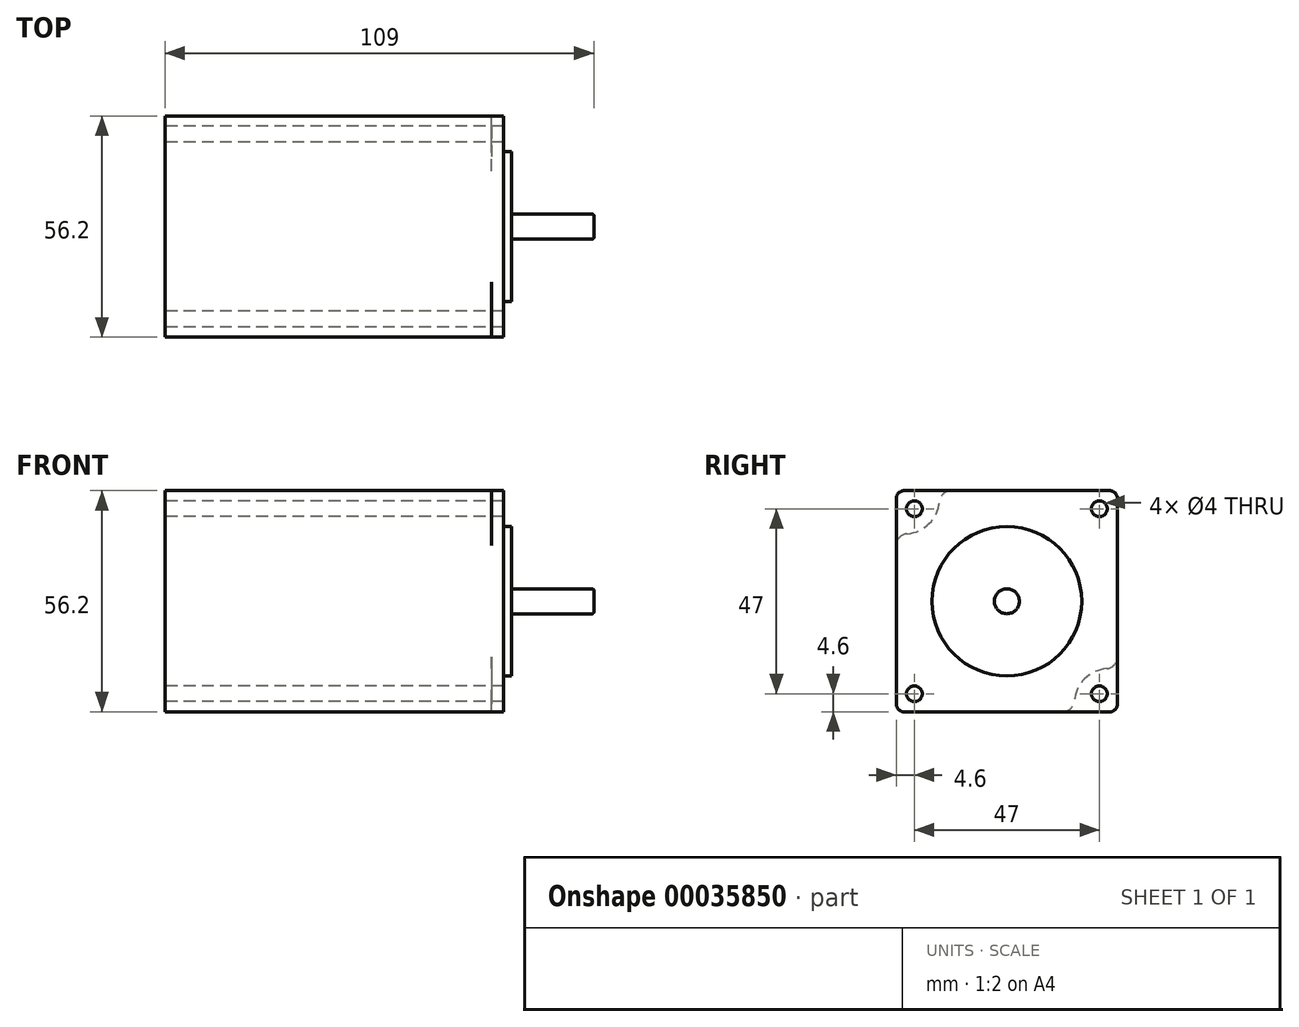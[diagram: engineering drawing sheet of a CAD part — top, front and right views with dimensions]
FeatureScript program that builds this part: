
annotation { "Feature Type Name" : "Feature", "Feature Type Description" : "" }
export const myFeature = defineFeature(function(context is Context, id is Id, definition is map)
    precondition{}
    {
        {
            var Q0;
            Q0=qCreatedBy(makeId("Right.planeOp"),FACE);
            var sketch = newSketch(context, id + "F0", { "sketchPlane" : qUnion([Q0])});
            skLineSegment(sketch, "E0.bottom", {"start": v(-26.1, 28.1) * mm, "end": v(26.1, 28.1) * mm});
            skLineSegment(sketch, "E0.top", {"start": v(-26.1, -28.1) * mm, "end": v(26.1, -28.1) * mm});
            skLineSegment(sketch, "E0.left", {"start": v(-28.1, 26.1) * mm, "end": v(-28.1, -26.1) * mm});
            skLineSegment(sketch, "E0.right", {"start": v(28.1, 26.1) * mm, "end": v(28.1, -26.1) * mm});
            skLineSegment(sketch, "E1", {"start": v(-28.1, 0) * mm, "end": v(28.1, 0) * mm, "construction": true});
            skLineSegment(sketch, "E2", {"start": v(0, 28.1) * mm, "end": v(0, -28.1) * mm, "construction": true});
            skCircle(sketch, "E3", {"center": v(-23.5, 23.5) * mm, "radius": 2 * mm});
            skCircle(sketch, "E4.0.MirrorC", {"center": v(23.5, 23.5) * mm, "radius": 2 * mm});
            skCircle(sketch, "E5.0.MirrorC", {"center": v(23.5, -23.5) * mm, "radius": 2 * mm});
            skCircle(sketch, "E6.0.MirrorC", {"center": v(-23.5, -23.5) * mm, "radius": 2 * mm});
            skPoint(sketch, "E7.visualSharp", {"position": v(-28.1, 28.1) * mm});
            skArc(sketch, "E7.filletArc", {"start": v(-26.1, 28.1) * mm, "mid": v(-27.51, 27.51) * mm, "end": v(-28.1, 26.1) * mm});
            skPoint(sketch, "E8.visualSharp", {"position": v(28.1, 28.1) * mm});
            skArc(sketch, "E8.filletArc", {"start": v(28.1, 26.1) * mm, "mid": v(27.51, 27.51) * mm, "end": v(26.1, 28.1) * mm});
            skPoint(sketch, "E9.visualSharp", {"position": v(28.1, -28.1) * mm});
            skArc(sketch, "E9.filletArc", {"start": v(26.1, -28.1) * mm, "mid": v(27.51, -27.51) * mm, "end": v(28.1, -26.1) * mm});
            skPoint(sketch, "E10.visualSharp", {"position": v(-28.1, -28.1) * mm});
            skArc(sketch, "E10.filletArc", {"start": v(-28.1, -26.1) * mm, "mid": v(-27.51, -27.51) * mm, "end": v(-26.1, -28.1) * mm});
            skLineSegment(sketch, "E11", {"start": v(23.5, 23.5) * mm, "end": v(-23.5, 23.5) * mm, "construction": true});
            skLineSegment(sketch, "E12", {"start": v(-23.5, 23.5) * mm, "end": v(-23.5, -23.5) * mm, "construction": true});
            skLineSegment(sketch, "E13", {"start": v(28.1, 28.1) * mm, "end": v(-28.1, 28.1) * mm, "construction": true});
            skLineSegment(sketch, "E14", {"start": v(-28.1, -28.1) * mm, "end": v(-28.1, 28.1) * mm, "construction": true});
            skSolve(sketch);
        }
        {
            var Q0;
            Q0=makeQuery(id+"F0.imprint","IMPRINT",FACE,{"disambiguationData":[TD([[makeQuery(id+"F0.imprint","IMPRINT",EDGE,{"derivedFrom":sQuery(id+"F0.wireOp",EDGE,"E0.bottom")}),-1.0]])]});
            extrude(context, id + "F1", {"entities" : qUnion([Q0]), "depth" : 86 * mm});
        }
        {
            var Q0;
            Q0=makeQuery(id+"F1.opExtrude","CAP_FACE",FACE,{"disambiguationData":[OSD([sQuery(id+"F0.wireOp",EDGE,"E0.bottom"),sQuery(id+"F0.wireOp",EDGE,"E0.top"),sQuery(id+"F0.wireOp",EDGE,"E0.left"),sQuery(id+"F0.wireOp",EDGE,"E0.right"),sQuery(id+"F0.wireOp",EDGE,"E3"),sQuery(id+"F0.wireOp",EDGE,"E4.0.MirrorC"),sQuery(id+"F0.wireOp",EDGE,"E5.0.MirrorC"),sQuery(id+"F0.wireOp",EDGE,"E6.0.MirrorC"),sQuery(id+"F0.wireOp",EDGE,"E7.filletArc"),sQuery(id+"F0.wireOp",EDGE,"E8.filletArc"),sQuery(id+"F0.wireOp",EDGE,"E9.filletArc"),sQuery(id+"F0.wireOp",EDGE,"E10.filletArc"),sQuery(id+"F0.wireOp",EDGE,"ba6df332-af28-43ae-9241-533709e672ff")])],"isStart":false});
            var sketch = newSketch(context, id + "F2", { "sketchPlane" : qUnion([Q0])});
            skCircle(sketch, "E15", {"center": v(0, 0) * mm, "radius": 19 * mm});
            skSolve(sketch);
        }
        {
            var Q0;
            {var subQ0=makeQuery(id+"F2.imprint","IMPRINT",EDGE,{"derivedFrom":makeQuery(id+"F1.opExtrude","CAP_EDGE",EDGE,{"disambiguationData":[OSD([sQuery(id+"F0.wireOp",EDGE,"ba6df332-af28-43ae-9241-533709e672ff")])],"isStart":false})});Q0=qUnion([makeQuery(id+"F2.imprint","IMPRINT",FACE,{"disambiguationData":[TD([[subQ0,1.0]])]}),makeQuery(id+"F2.imprint","IMPRINT",FACE,{"disambiguationData":[TD([[makeQuery(id+"F2.imprint","IMPRINT",EDGE,{"derivedFrom":sQuery(id+"F2.wireOp",EDGE,"E15")}),1.0]])]})]);}
            extrude(context, id + "F3", {"entities" : qUnion([Q0]), "operationType" : NewBodyOperationType.ADD, "depth" : 2 * mm});
        }
        {
            var Q0;
            Q0=makeQuery(id+"F3.opExtrude","CAP_FACE",FACE,{"disambiguationData":[OSD([sQuery(id+"F2.wireOp",EDGE,"E15")])],"isStart":false});
            var sketch = newSketch(context, id + "F4", { "sketchPlane" : qUnion([Q0])});
            skCircle(sketch, "E16", {"center": v(0, 0) * mm, "radius": 3.17 * mm});
            skSolve(sketch);
        }
        {
            var Q0;
            Q0=makeQuery(id+"F4.imprint","IMPRINT",FACE,{"disambiguationData":[TD([[makeQuery(id+"F4.imprint","IMPRINT",EDGE,{"derivedFrom":sQuery(id+"F4.wireOp",EDGE,"E16")}),1.0]])]});
            extrude(context, id + "F5", {"entities" : qUnion([Q0]), "operationType" : NewBodyOperationType.ADD, "depth" : 21 * mm});
        }
        {
            var Q0;
            Q0=makeQuery(id+"F5.opExtrude","CAP_EDGE",EDGE,{"disambiguationData":[OSD([sQuery(id+"F4.wireOp",EDGE,"E16")])],"isStart":false});
            fillet(context, id + "F6", {"entities" : qUnion([Q0]), "radius" : 0.5 * mm, "tangentPropagation" : true, "allowEdgeOverflow" : false});
        }
        {
            var Q0;
            Q0=makeQuery(id+"F1.opExtrude","CAP_FACE",FACE,{"disambiguationData":[OSD([sQuery(id+"F0.wireOp",EDGE,"E0.bottom"),sQuery(id+"F0.wireOp",EDGE,"E0.top"),sQuery(id+"F0.wireOp",EDGE,"E0.left"),sQuery(id+"F0.wireOp",EDGE,"E0.right"),sQuery(id+"F0.wireOp",EDGE,"E3"),sQuery(id+"F0.wireOp",EDGE,"E4.0.MirrorC"),sQuery(id+"F0.wireOp",EDGE,"E5.0.MirrorC"),sQuery(id+"F0.wireOp",EDGE,"E6.0.MirrorC"),sQuery(id+"F0.wireOp",EDGE,"E7.filletArc"),sQuery(id+"F0.wireOp",EDGE,"E8.filletArc"),sQuery(id+"F0.wireOp",EDGE,"E9.filletArc"),sQuery(id+"F0.wireOp",EDGE,"E10.filletArc"),sQuery(id+"F0.wireOp",EDGE,"ba6df332-af28-43ae-9241-533709e672ff")])],"isStart":false});
            cPlane(context, id + "F7", {"entities" : qUnion([Q0]), "cplaneType" : CPlaneType.OFFSET, "offset" : 3 * mm, "oppositeDirection" : true, "width" : 150 * mm, "height" : 150 * mm});
        }
        {
            var Q0;
            Q0=qCreatedBy(id+"F7.planeOp",FACE);
            var sketch = newSketch(context, id + "F8", { "sketchPlane" : qUnion([Q0])});
            skCircle(sketch, "E17", {"center": v(-26.1, 26.1) * mm, "radius": 9 * mm});
            skCircle(sketch, "E18.0.MirrorC", {"center": v(26.1, 26.1) * mm, "radius": 9 * mm});
            skCircle(sketch, "E19.0.MirrorC", {"center": v(-26.1, -26.1) * mm, "radius": 9 * mm});
            skCircle(sketch, "E20.0.MirrorC", {"center": v(26.1, -26.1) * mm, "radius": 9 * mm});
            skSolve(sketch);
        }
        {
            var Q0;
            {Q0=qUnion([makeQuery(id+"F8.imprint","IMPRINT",FACE,{"disambiguationData":[TD([[makeQuery(id+"F8.imprint","IMPRINT",EDGE,{"derivedFrom":sQuery(id+"F8.wireOp",EDGE,"E17")}),1.0]])]}),makeQuery(id+"F8.imprint","IMPRINT",FACE,{"disambiguationData":[TD([[makeQuery(id+"F8.imprint","IMPRINT",EDGE,{"derivedFrom":sQuery(id+"F8.wireOp",EDGE,"E18.0.MirrorC")}),-1.0]])]}),makeQuery(id+"F8.imprint","IMPRINT",FACE,{"disambiguationData":[TD([[makeQuery(id+"F8.imprint","IMPRINT",EDGE,{"derivedFrom":sQuery(id+"F8.wireOp",EDGE,"E19.0.MirrorC")}),-1.0]])]}),makeQuery(id+"F8.imprint","IMPRINT",FACE,{"disambiguationData":[TD([[makeQuery(id+"F8.imprint","IMPRINT",EDGE,{"derivedFrom":sQuery(id+"F8.wireOp",EDGE,"E20.0.MirrorC")}),1.0]])]})]);}
            var Q1;
            Q1=makeQuery(id+"F1.opExtrude","CAP_FACE",FACE,{"disambiguationData":[OSD([sQuery(id+"F0.wireOp",EDGE,"E0.bottom"),sQuery(id+"F0.wireOp",EDGE,"E0.top"),sQuery(id+"F0.wireOp",EDGE,"E0.left"),sQuery(id+"F0.wireOp",EDGE,"E0.right"),sQuery(id+"F0.wireOp",EDGE,"E3"),sQuery(id+"F0.wireOp",EDGE,"E4.0.MirrorC"),sQuery(id+"F0.wireOp",EDGE,"E5.0.MirrorC"),sQuery(id+"F0.wireOp",EDGE,"E6.0.MirrorC"),sQuery(id+"F0.wireOp",EDGE,"E7.filletArc"),sQuery(id+"F0.wireOp",EDGE,"E8.filletArc"),sQuery(id+"F0.wireOp",EDGE,"E9.filletArc"),sQuery(id+"F0.wireOp",EDGE,"E10.filletArc"),sQuery(id+"F0.wireOp",EDGE,"ba6df332-af28-43ae-9241-533709e672ff")])],"isStart":true});
            extrude(context, id + "F9", {"entities" : qUnion([Q0]), "operationType" : NewBodyOperationType.REMOVE, "endBound" : BoundingType.UP_TO_SURFACE, "oppositeDirection" : true, "endBoundEntityFace" : qUnion([Q1]), "depth" : 25 * mm});
        }
        {
            var Q0;
            Q0=makeQuery(id+"F9.boolean.opBoolean","INTERSECT",EDGE,{"derivedFrom":[makeQuery(id+"F1.opExtrude","SWEPT_FACE",FACE,{"disambiguationData":[OSD([sQuery(id+"F0.wireOp",EDGE,"E0.bottom")])]}),makeQuery(id+"F9.opExtrude","SWEPT_FACE",FACE,{"disambiguationData":[OSD([sQuery(id+"F8.wireOp",EDGE,"E18.0.MirrorC")])]})]});
            var Q1;
            Q1=makeQuery(id+"F9.boolean.opBoolean","INTERSECT",EDGE,{"derivedFrom":[makeQuery(id+"F1.opExtrude","SWEPT_FACE",FACE,{"disambiguationData":[OSD([sQuery(id+"F0.wireOp",EDGE,"E0.right")])]}),makeQuery(id+"F9.opExtrude","SWEPT_FACE",FACE,{"disambiguationData":[OSD([sQuery(id+"F8.wireOp",EDGE,"E18.0.MirrorC")])]})]});
            var Q2;
            Q2=makeQuery(id+"F9.boolean.opBoolean","INTERSECT",EDGE,{"derivedFrom":[makeQuery(id+"F1.opExtrude","SWEPT_FACE",FACE,{"disambiguationData":[OSD([sQuery(id+"F0.wireOp",EDGE,"E0.bottom")])]}),makeQuery(id+"F9.opExtrude","SWEPT_FACE",FACE,{"disambiguationData":[OSD([sQuery(id+"F8.wireOp",EDGE,"E17")])]})]});
            var Q3;
            Q3=makeQuery(id+"F9.boolean.opBoolean","INTERSECT",EDGE,{"derivedFrom":[makeQuery(id+"F1.opExtrude","SWEPT_FACE",FACE,{"disambiguationData":[OSD([sQuery(id+"F0.wireOp",EDGE,"E0.left")])]}),makeQuery(id+"F9.opExtrude","SWEPT_FACE",FACE,{"disambiguationData":[OSD([sQuery(id+"F8.wireOp",EDGE,"E17")])]})]});
            var Q4;
            Q4=makeQuery(id+"F9.boolean.opBoolean","INTERSECT",EDGE,{"derivedFrom":[makeQuery(id+"F1.opExtrude","SWEPT_FACE",FACE,{"disambiguationData":[OSD([sQuery(id+"F0.wireOp",EDGE,"E0.left")])]}),makeQuery(id+"F9.opExtrude","SWEPT_FACE",FACE,{"disambiguationData":[OSD([sQuery(id+"F8.wireOp",EDGE,"E19.0.MirrorC")])]})]});
            var Q5;
            Q5=makeQuery(id+"F9.boolean.opBoolean","INTERSECT",EDGE,{"derivedFrom":[makeQuery(id+"F1.opExtrude","SWEPT_FACE",FACE,{"disambiguationData":[OSD([sQuery(id+"F0.wireOp",EDGE,"E0.top")])]}),makeQuery(id+"F9.opExtrude","SWEPT_FACE",FACE,{"disambiguationData":[OSD([sQuery(id+"F8.wireOp",EDGE,"E19.0.MirrorC")])]})]});
            var Q6;
            Q6=makeQuery(id+"F9.boolean.opBoolean","INTERSECT",EDGE,{"derivedFrom":[makeQuery(id+"F1.opExtrude","SWEPT_FACE",FACE,{"disambiguationData":[OSD([sQuery(id+"F0.wireOp",EDGE,"E0.top")])]}),makeQuery(id+"F9.opExtrude","SWEPT_FACE",FACE,{"disambiguationData":[OSD([sQuery(id+"F8.wireOp",EDGE,"E20.0.MirrorC")])]})]});
            var Q7;
            Q7=makeQuery(id+"F9.boolean.opBoolean","INTERSECT",EDGE,{"derivedFrom":[makeQuery(id+"F1.opExtrude","SWEPT_FACE",FACE,{"disambiguationData":[OSD([sQuery(id+"F0.wireOp",EDGE,"E0.right")])]}),makeQuery(id+"F9.opExtrude","SWEPT_FACE",FACE,{"disambiguationData":[OSD([sQuery(id+"F8.wireOp",EDGE,"E20.0.MirrorC")])]})]});
            fillet(context, id + "F10", {"entities" : qUnion([Q0, Q1, Q2, Q3, Q4, Q5, Q6, Q7]), "radius" : 3 * mm, "tangentPropagation" : true, "allowEdgeOverflow" : false});
        }
    });
